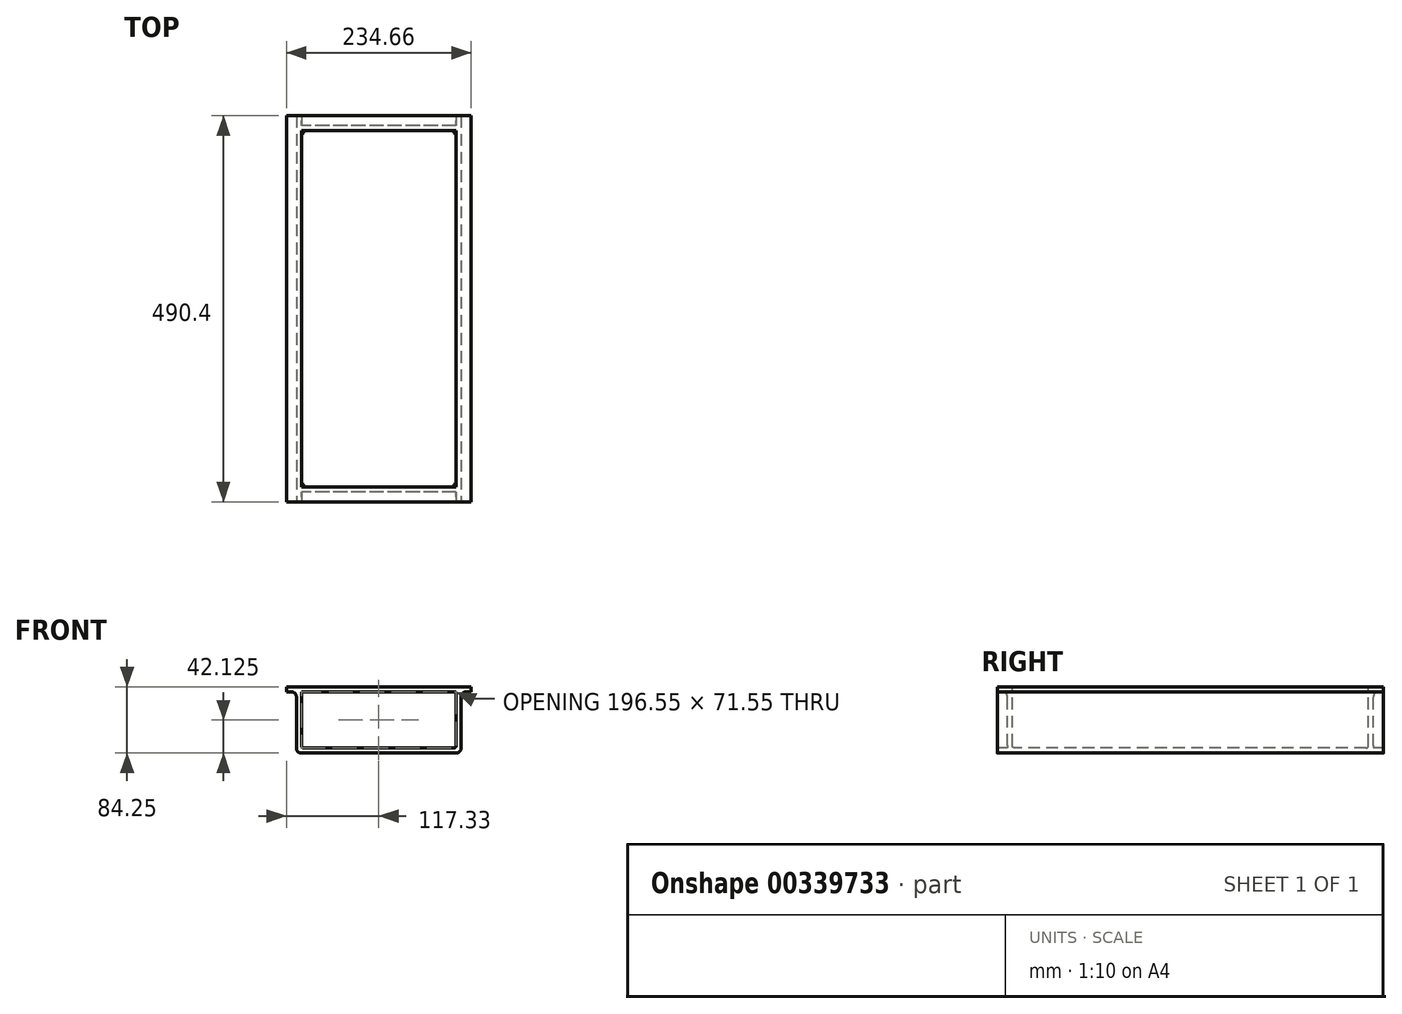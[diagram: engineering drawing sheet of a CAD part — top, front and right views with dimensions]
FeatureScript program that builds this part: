
annotation { "Feature Type Name" : "Feature", "Feature Type Description" : "" }
export const myFeature = defineFeature(function(context is Context, id is Id, definition is map)
    precondition{}
    {
        {
            var Q0;
            Q0=qCreatedBy(makeId("Top.planeOp"),FACE);
            var sketch = newSketch(context, id + "F0", { "sketchPlane" : qUnion([Q0])});
            skLineSegment(sketch, "E0.bottom", {"start": v(100.43, -232.5) * mm, "end": v(-100.43, -232.5) * mm, "construction": true});
            skLineSegment(sketch, "E0.top", {"start": v(100.43, 232.5) * mm, "end": v(-100.43, 232.5) * mm, "construction": true});
            skLineSegment(sketch, "E0.left", {"start": v(104.63, -228.3) * mm, "end": v(104.62, 228.3) * mm, "construction": true});
            skLineSegment(sketch, "E0.right", {"start": v(-104.62, -228.3) * mm, "end": v(-104.63, 228.3) * mm, "construction": true});
            skPoint(sketch, "E0.middle", {"position": v(0, 0) * mm});
            skPoint(sketch, "E1.visualSharp", {"position": v(-104.63, 232.5) * mm});
            skArc(sketch, "E1.filletArc", {"start": v(-100.43, 232.5) * mm, "mid": v(-103.4, 231.27) * mm, "end": v(-104.63, 228.3) * mm, "construction": true});
            skPoint(sketch, "E2.visualSharp", {"position": v(104.62, 232.5) * mm});
            skArc(sketch, "E2.filletArc", {"start": v(104.62, 228.3) * mm, "mid": v(103.4, 231.27) * mm, "end": v(100.43, 232.5) * mm, "construction": true});
            skPoint(sketch, "E3.visualSharp", {"position": v(104.63, -232.5) * mm});
            skArc(sketch, "E3.filletArc", {"start": v(100.43, -232.5) * mm, "mid": v(103.4, -231.27) * mm, "end": v(104.63, -228.3) * mm, "construction": true});
            skPoint(sketch, "E4.visualSharp", {"position": v(-104.62, -232.5) * mm});
            skArc(sketch, "E4.filletArc", {"start": v(-104.62, -228.3) * mm, "mid": v(-103.4, -231.27) * mm, "end": v(-100.43, -232.5) * mm, "construction": true});
            skPoint(sketch, "E5.visualSharp", {"position": v(-98.28, 226.15) * mm});
            skPoint(sketch, "E6.visualSharp", {"position": v(98.27, 226.15) * mm});
            skPoint(sketch, "E7.visualSharp", {"position": v(98.28, -226.15) * mm});
            skPoint(sketch, "E8.visualSharp", {"position": v(-98.27, -226.15) * mm});
            skArc(sketch, "E9.0", {"start": v(100.43, -245.2) * mm, "mid": v(112.38, -240.25) * mm, "end": v(117.33, -228.3) * mm});
            skLineSegment(sketch, "E9.1", {"start": v(100.43, -245.2) * mm, "end": v(-100.43, -245.2) * mm});
            skLineSegment(sketch, "E9.2", {"start": v(117.33, -228.3) * mm, "end": v(117.32, 228.3) * mm});
            skArc(sketch, "E9.3", {"start": v(-117.32, -228.3) * mm, "mid": v(-112.38, -240.25) * mm, "end": v(-100.43, -245.2) * mm});
            skArc(sketch, "E9.4", {"start": v(117.32, 228.3) * mm, "mid": v(112.38, 240.25) * mm, "end": v(100.43, 245.2) * mm});
            skLineSegment(sketch, "E9.5", {"start": v(100.43, 245.2) * mm, "end": v(-100.43, 245.2) * mm});
            skArc(sketch, "E9.6", {"start": v(-100.43, 245.2) * mm, "mid": v(-112.38, 240.25) * mm, "end": v(-117.33, 228.3) * mm});
            skLineSegment(sketch, "E9.7", {"start": v(-117.32, -228.3) * mm, "end": v(-117.33, 228.3) * mm});
            skSolve(sketch);
        }
        {
            var Q0;
            Q0=qCreatedBy(makeId("Front.planeOp"),FACE);
            var sketch = newSketch(context, id + "F1", { "sketchPlane" : qUnion([Q0])});
            skLineSegment(sketch, "E10.bottom", {"start": v(-104.62, 0) * mm, "end": v(-98.27, 0) * mm});
            skLineSegment(sketch, "E10.top", {"start": v(-98.27, -84.25) * mm, "end": v(98.27, -84.25) * mm});
            skLineSegment(sketch, "E10.left", {"start": v(-104.62, -12.7) * mm, "end": v(-104.62, -77.9) * mm});
            skLineSegment(sketch, "E10.right", {"start": v(104.62, -12.7) * mm, "end": v(104.62, -77.9) * mm});
            skPoint(sketch, "E11.visualSharp", {"position": v(-104.62, -84.25) * mm});
            skArc(sketch, "E11.filletArc", {"start": v(-104.62, -77.9) * mm, "mid": v(-102.77, -82.4) * mm, "end": v(-98.27, -84.25) * mm});
            skPoint(sketch, "E12.visualSharp", {"position": v(104.62, -84.25) * mm});
            skArc(sketch, "E12.filletArc", {"start": v(98.27, -84.25) * mm, "mid": v(102.77, -82.4) * mm, "end": v(104.62, -77.9) * mm});
            skLineSegment(sketch, "E13.bottom", {"start": v(-117.32, 0) * mm, "end": v(-104.62, 0) * mm});
            skLineSegment(sketch, "E13.top", {"start": v(-117.32, -6.35) * mm, "end": v(-110.97, -6.35) * mm});
            skLineSegment(sketch, "E13.left", {"start": v(-117.32, 0) * mm, "end": v(-117.32, -6.35) * mm});
            skLineSegment(sketch, "E13.right", {"start": v(117.32, 0) * mm, "end": v(117.32, -6.35) * mm});
            skLineSegment(sketch, "E14.trimOffspring", {"start": v(110.97, -6.35) * mm, "end": v(117.32, -6.35) * mm});
            skPoint(sketch, "E15.visualSharp", {"position": v(-104.62, -6.35) * mm});
            skArc(sketch, "E15.filletArc", {"start": v(-104.62, -12.7) * mm, "mid": v(-106.48, -8.2) * mm, "end": v(-110.97, -6.35) * mm});
            skPoint(sketch, "E16.visualSharp", {"position": v(104.62, -6.35) * mm});
            skArc(sketch, "E16.filletArc", {"start": v(110.97, -6.35) * mm, "mid": v(106.48, -8.2) * mm, "end": v(104.62, -12.7) * mm});
            skLineSegment(sketch, "E17.0", {"start": v(98.27, 0) * mm, "end": v(98.27, -74.73) * mm});
            skLineSegment(sketch, "E17.1", {"start": v(-95.1, -77.9) * mm, "end": v(95.1, -77.9) * mm});
            skLineSegment(sketch, "E17.2", {"start": v(-98.27, 0) * mm, "end": v(-98.27, -74.73) * mm});
            skLineSegment(sketch, "E18.trimOffspring", {"start": v(98.27, 0) * mm, "end": v(117.32, 0) * mm});
            skLineSegment(sketch, "E19.trimOffspring", {"start": v(98.28, 0) * mm, "end": v(104.62, 0) * mm});
            skArc(sketch, "E20.filletArc", {"start": v(-98.27, -74.73) * mm, "mid": v(-97.35, -76.97) * mm, "end": v(-95.1, -77.9) * mm});
            skArc(sketch, "E21.filletArc", {"start": v(95.1, -77.9) * mm, "mid": v(97.35, -76.97) * mm, "end": v(98.27, -74.73) * mm});
            skSolve(sketch);
        }
        {
            var Q0;
            Q0=qCreatedBy(makeId("Right.planeOp"),FACE);
            var sketch = newSketch(context, id + "F2", { "sketchPlane" : qUnion([Q0])});
            skLineSegment(sketch, "E22.bottom", {"start": v(-232.5, 0) * mm, "end": v(-226.15, 0) * mm});
            skLineSegment(sketch, "E22.top", {"start": v(-226.15, -84.25) * mm, "end": v(226.15, -84.25) * mm});
            skLineSegment(sketch, "E22.left", {"start": v(-232.5, -12.7) * mm, "end": v(-232.5, -77.9) * mm});
            skLineSegment(sketch, "E22.right", {"start": v(232.5, -12.7) * mm, "end": v(232.5, -77.9) * mm});
            skPoint(sketch, "E23.visualSharp", {"position": v(232.5, -84.25) * mm});
            skArc(sketch, "E23.filletArc", {"start": v(226.15, -84.25) * mm, "mid": v(230.64, -82.4) * mm, "end": v(232.5, -77.9) * mm});
            skPoint(sketch, "E24.visualSharp", {"position": v(-232.5, -84.25) * mm});
            skArc(sketch, "E24.filletArc", {"start": v(-232.5, -77.9) * mm, "mid": v(-230.64, -82.4) * mm, "end": v(-226.15, -84.25) * mm});
            skLineSegment(sketch, "E25.bottom", {"start": v(-245.2, 0) * mm, "end": v(-226.15, 0) * mm});
            skLineSegment(sketch, "E25.top", {"start": v(-245.2, -6.35) * mm, "end": v(-238.85, -6.35) * mm});
            skLineSegment(sketch, "E25.left", {"start": v(-245.2, 0) * mm, "end": v(-245.2, -6.35) * mm});
            skLineSegment(sketch, "E25.right", {"start": v(245.2, 0) * mm, "end": v(245.2, -6.35) * mm});
            skLineSegment(sketch, "E26.trimOffspring", {"start": v(238.85, -6.35) * mm, "end": v(245.2, -6.35) * mm});
            skPoint(sketch, "E27.visualSharp", {"position": v(-232.5, -6.35) * mm});
            skArc(sketch, "E27.filletArc", {"start": v(-232.5, -12.7) * mm, "mid": v(-234.36, -8.2) * mm, "end": v(-238.85, -6.35) * mm});
            skPoint(sketch, "E28.visualSharp", {"position": v(232.5, -6.35) * mm});
            skArc(sketch, "E28.filletArc", {"start": v(238.85, -6.35) * mm, "mid": v(234.36, -8.2) * mm, "end": v(232.5, -12.7) * mm});
            skLineSegment(sketch, "E29.0", {"start": v(-226.15, 0) * mm, "end": v(-226.15, -74.72) * mm});
            skLineSegment(sketch, "E29.1", {"start": v(-222.98, -77.9) * mm, "end": v(222.98, -77.9) * mm});
            skLineSegment(sketch, "E29.2", {"start": v(226.15, 0) * mm, "end": v(226.15, -74.72) * mm});
            skLineSegment(sketch, "E30.trimOffspring", {"start": v(226.15, 0) * mm, "end": v(245.2, 0) * mm});
            skLineSegment(sketch, "E31.trimOffspring", {"start": v(226.15, 0) * mm, "end": v(232.5, 0) * mm});
            skArc(sketch, "E32.filletArc", {"start": v(222.98, -77.9) * mm, "mid": v(225.22, -76.97) * mm, "end": v(226.15, -74.72) * mm});
            skArc(sketch, "E33.filletArc", {"start": v(-226.15, -74.72) * mm, "mid": v(-225.22, -76.97) * mm, "end": v(-222.98, -77.9) * mm});
            skSolve(sketch);
        }
        {
            var Q0;
            Q0=makeQuery(id+"F1.imprint","IMPRINT",FACE,{"disambiguationData":[TD([[makeQuery(id+"F1.imprint","IMPRINT",EDGE,{"derivedFrom":sQuery(id+"F1.wireOp",EDGE,"E10.bottom")}),-1.0]])]});
            var Q1;
            Q1=sQuery(id+"F2.wireOp",VERTEX,"E25.right.end");
            var Q2;
            Q2=sQuery(id+"F2.wireOp",VERTEX,"E25.top.start");
            extrude(context, id + "F3", {"entities" : qUnion([Q0]), "endBound" : BoundingType.UP_TO_VERTEX, "oppositeDirection" : true, "endBoundEntityVertex" : qUnion([Q1]), "depth" : 25.4 * mm, "hasSecondDirection" : true, "secondDirectionBound" : SecondDirectionBoundingType.UP_TO_VERTEX, "secondDirectionOppositeDirection" : false, "secondDirectionBoundEntityVertex" : qUnion([Q2]), "secondDirectionDepth" : 25.4 * mm});
        }
        {
            var Q0;
            Q0=makeQuery(id+"F2.imprint","IMPRINT",FACE,{"disambiguationData":[TD([[makeQuery(id+"F2.imprint","IMPRINT",EDGE,{"derivedFrom":sQuery(id+"F2.wireOp",EDGE,"E22.top")}),1.0]])]});
            var Q1;
            Q1=makeQuery(id+"F3.opExtrude","SWEPT_FACE",FACE,{"disambiguationData":[OSD([sQuery(id+"F1.wireOp",EDGE,"E17.0")])]});
            var Q2;
            Q2=makeQuery(id+"F3.opExtrude","SWEPT_FACE",FACE,{"disambiguationData":[OSD([sQuery(id+"F1.wireOp",EDGE,"E17.2")])]});
            extrude(context, id + "F4", {"entities" : qUnion([Q0]), "operationType" : NewBodyOperationType.ADD, "endBound" : BoundingType.UP_TO_SURFACE, "endBoundEntityFace" : qUnion([Q1]), "depth" : 25.4 * mm, "hasSecondDirection" : true, "secondDirectionBound" : SecondDirectionBoundingType.UP_TO_SURFACE, "secondDirectionOppositeDirection" : true, "secondDirectionBoundEntityFace" : qUnion([Q2]), "secondDirectionDepth" : 25.4 * mm});
        }
    });
